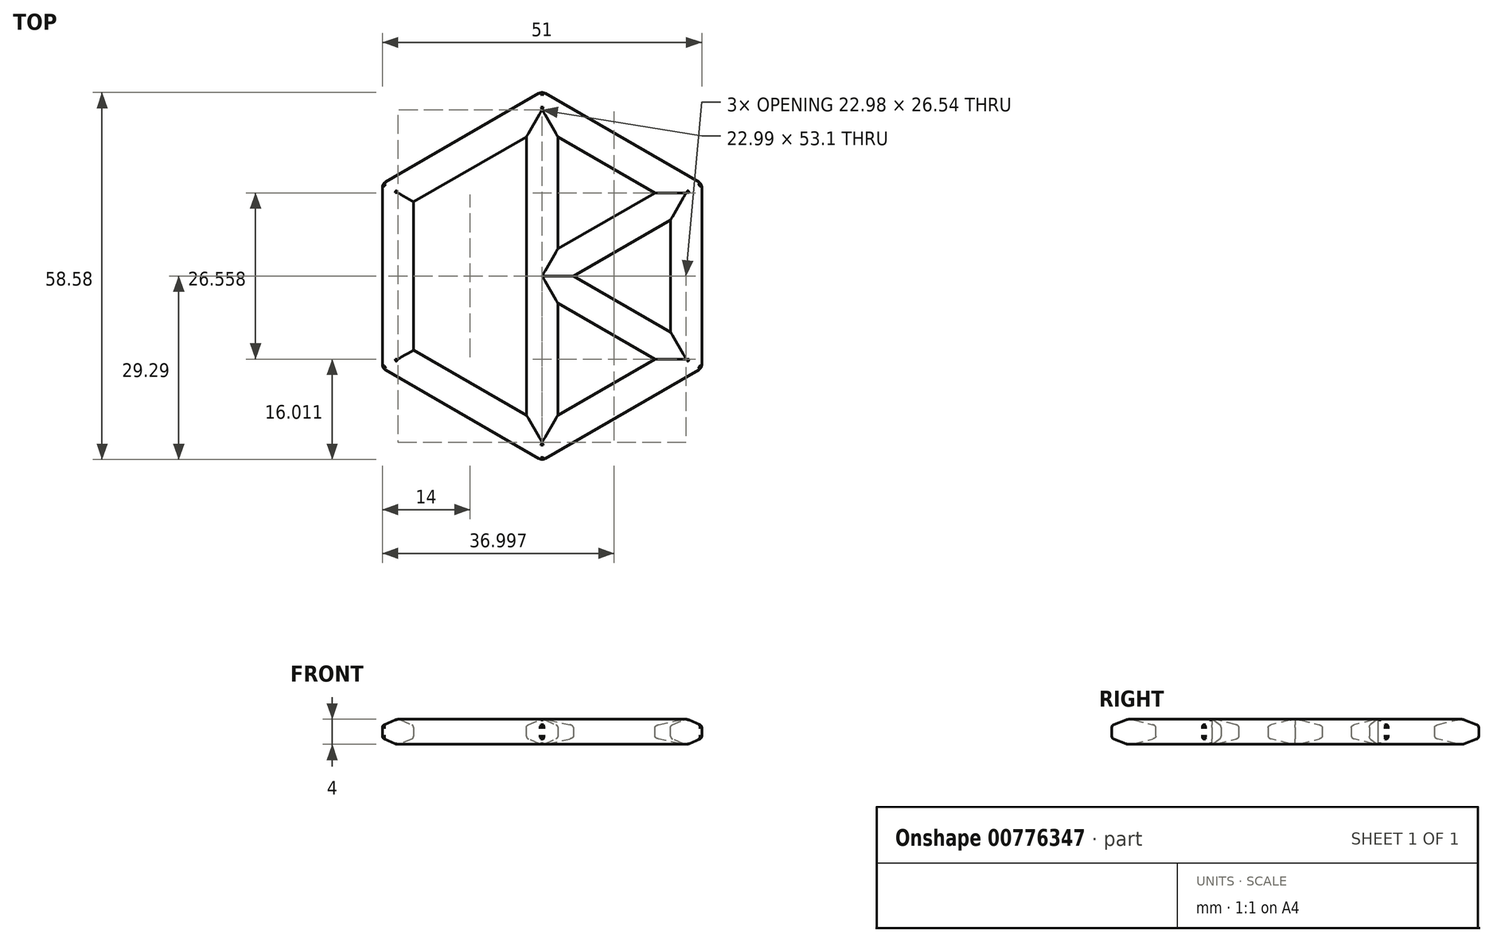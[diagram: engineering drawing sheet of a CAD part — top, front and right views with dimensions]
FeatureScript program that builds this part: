
annotation { "Feature Type Name" : "Feature", "Feature Type Description" : "" }
export const myFeature = defineFeature(function(context is Context, id is Id, definition is map)
    precondition{}
    {
        {
            var Q0;
            Q0=qCreatedBy(makeId("Top.planeOp"),FACE);
            var sketch = newSketch(context, id + "F0", { "sketchPlane" : qUnion([Q0])});
            skCircle(sketch, "E0.cCircle", {"center": v(0, 0) * mm, "radius": 25.5 * mm, "construction": true});
            skLineSegment(sketch, "E0.0", {"start": v(-25.5, -14.72) * mm, "end": v(-25.5, 14.72) * mm});
            skLineSegment(sketch, "E0.1", {"start": v(-25.5, 14.72) * mm, "end": v(0, 29.44) * mm});
            skLineSegment(sketch, "E0.2", {"start": v(0, 29.44) * mm, "end": v(25.5, 14.72) * mm});
            skLineSegment(sketch, "E0.3", {"start": v(25.5, 14.72) * mm, "end": v(25.5, -14.72) * mm});
            skLineSegment(sketch, "E0.4", {"start": v(25.5, -14.72) * mm, "end": v(0, -29.44) * mm});
            skLineSegment(sketch, "E0.5", {"start": v(0, -29.44) * mm, "end": v(-25.5, -14.72) * mm});
            skPoint(sketch, "E0.0.midPoint", {"position": v(-25.5, 0) * mm});
            skSolve(sketch);
        }
        {
            var Q0;
            Q0=qCreatedBy(makeId("Front.planeOp"),FACE);
            var sketch = newSketch(context, id + "F1", { "sketchPlane" : qUnion([Q0])});
            skLineSegment(sketch, "E1", {"start": v(-25.5, -1) * mm, "end": v(-25.5, 1) * mm});
            skLineSegment(sketch, "E2", {"start": v(-22.75, 2) * mm, "end": v(-20.5, 1) * mm});
            skLineSegment(sketch, "E3", {"start": v(-20.5, 1) * mm, "end": v(-20.5, -1) * mm});
            skLineSegment(sketch, "E4", {"start": v(-20.5, -1) * mm, "end": v(-22.75, -2) * mm});
            skLineSegment(sketch, "E5", {"start": v(-23.25, 2) * mm, "end": v(-23.25, -2) * mm});
            skLineSegment(sketch, "E6", {"start": v(-22.75, -2) * mm, "end": v(-22.75, 2) * mm});
            skLineSegment(sketch, "E7", {"start": v(-25.5, -1) * mm, "end": v(-23.25, -2) * mm});
            skLineSegment(sketch, "E8", {"start": v(-22.75, -2) * mm, "end": v(-23.25, -2) * mm});
            skLineSegment(sketch, "E9", {"start": v(-23.25, 2) * mm, "end": v(-22.75, 2) * mm});
            skLineSegment(sketch, "E10", {"start": v(-25.5, 1) * mm, "end": v(-23.25, 2) * mm});
            skLineSegment(sketch, "E11", {"start": v(-22.75, 2) * mm, "end": v(-23.25, -2) * mm});
            skPoint(sketch, "E12", {"position": v(-23, 0) * mm});
            skSolve(sketch);
        }
        {
            var Q0;
            Q0=makeQuery(id+"F1.imprint","IMPRINT",FACE,{"disambiguationData":[TD([[makeQuery(id+"F1.imprint","IMPRINT",EDGE,{"derivedFrom":sQuery(id+"F1.wireOp",EDGE,"E1")}),-1.0]])]});
            var Q1;
            Q1=makeQuery(id+"F1.imprint","IMPRINT",FACE,{"disambiguationData":[TD([[makeQuery(id+"F1.imprint","IMPRINT",EDGE,{"derivedFrom":sQuery(id+"F1.wireOp",EDGE,"E5")}),1.0]])]});
            var Q2;
            Q2=makeQuery(id+"F1.imprint","IMPRINT",FACE,{"disambiguationData":[TD([[makeQuery(id+"F1.imprint","IMPRINT",EDGE,{"derivedFrom":sQuery(id+"F1.wireOp",EDGE,"E6")}),1.0]])]});
            var Q3;
            Q3=makeQuery(id+"F1.imprint","IMPRINT",FACE,{"disambiguationData":[TD([[makeQuery(id+"F1.imprint","IMPRINT",EDGE,{"derivedFrom":sQuery(id+"F1.wireOp",EDGE,"E2")}),-1.0]])]});
            var Q4;
            Q4=sQuery(id+"F0.wireOp",EDGE,"E0.3");
            var Q5;
            Q5=sQuery(id+"F0.wireOp",EDGE,"E0.2");
            var Q6;
            Q6=sQuery(id+"F0.wireOp",EDGE,"E0.1");
            var Q7;
            Q7=sQuery(id+"F0.wireOp",EDGE,"E0.0");
            var Q8;
            Q8=sQuery(id+"F0.wireOp",EDGE,"E0.5");
            var Q9;
            Q9=sQuery(id+"F0.wireOp",EDGE,"E0.4");
            sweep(context, id + "F2", {"profiles" : qUnion([Q0, Q1, Q2, Q3]), "path" : qUnion([Q4, Q5, Q6, Q7, Q8, Q9])});
        }
        {
            var Q0;
            Q0=qCreatedBy(makeId("Front.planeOp"),FACE);
            var sketch = newSketch(context, id + "F3", { "sketchPlane" : qUnion([Q0])});
            skLineSegment(sketch, "E13", {"start": v(-2.5, -1) * mm, "end": v(-2.5, 1) * mm});
            skLineSegment(sketch, "E14", {"start": v(0.25, 2) * mm, "end": v(2.5, 1) * mm});
            skLineSegment(sketch, "E15", {"start": v(2.5, 1) * mm, "end": v(2.5, -1) * mm});
            skLineSegment(sketch, "E16", {"start": v(2.5, -1) * mm, "end": v(0.25, -2) * mm});
            skLineSegment(sketch, "E17", {"start": v(-0.25, 2) * mm, "end": v(-0.25, -2) * mm});
            skLineSegment(sketch, "E18", {"start": v(0.25, -2) * mm, "end": v(0.25, 2) * mm});
            skLineSegment(sketch, "E19", {"start": v(-2.5, -1) * mm, "end": v(-0.25, -2) * mm});
            skLineSegment(sketch, "E20", {"start": v(0.25, -2) * mm, "end": v(-0.25, -2) * mm});
            skLineSegment(sketch, "E21", {"start": v(-0.25, 2) * mm, "end": v(0.25, 2) * mm});
            skLineSegment(sketch, "E22", {"start": v(-2.5, 1) * mm, "end": v(-0.25, 2) * mm});
            skLineSegment(sketch, "E23", {"start": v(0, 2) * mm, "end": v(0, -2) * mm});
            skPoint(sketch, "E24", {"position": v(0, 0) * mm});
            skSolve(sketch);
        }
        {
            var Q0;
            Q0=qSketchRegion(id+"F3",true);
            extrude(context, id + "F4", {"entities" : qUnion([Q0]), "endBound" : BoundingType.UP_TO_NEXT, "depth" : 25 * mm, "offsetDistance" : 25 * mm});
        }
        {
            var Q0;
            Q0=makeQuery(id+"F4.opExtrude","SWEPT_BODY",BODY,{"disambiguationData":[OSD([sQuery(id+"F3.wireOp",EDGE,"E13"),sQuery(id+"F3.wireOp",EDGE,"E14"),sQuery(id+"F3.wireOp",EDGE,"E15"),sQuery(id+"F3.wireOp",EDGE,"E16"),sQuery(id+"F3.wireOp",EDGE,"E19"),sQuery(id+"F3.wireOp",EDGE,"E20"),sQuery(id+"F3.wireOp",EDGE,"E21"),sQuery(id+"F3.wireOp",EDGE,"E22")])]});
            var Q1;
            Q1=sQuery(id+"F3.wireOp",EDGE,"E23");
            circularPattern(context, id + "F5", {"operationType" : NewBodyOperationType.ADD, "entities" : qUnion([Q0]), "axis" : qUnion([Q1]), "angle" : 180 * degree, "instanceCount" : 4, "oppositeDirection" : true, "equalSpace" : true});
        }
        {
            var Q0;
            Q0=makeQuery(id+"F2.opSweep","MID_CAP_EDGE",EDGE,{"disambiguationData":[OSD([sQuery(id+"F0.wireOp",VERTEX,"E0.4.start"),sQuery(id+"F1.wireOp",EDGE,"E1")])],"capPos":2.0});
            var Q1;
            Q1=makeQuery(id+"F2.opSweep","MID_CAP_EDGE",EDGE,{"disambiguationData":[OSD([sQuery(id+"F0.wireOp",VERTEX,"E0.4.start"),sQuery(id+"F1.wireOp",EDGE,"E10")])],"capPos":2.0});
            var Q2;
            Q2=makeQuery(id+"F2.opSweep","MID_CAP_EDGE",EDGE,{"disambiguationData":[OSD([sQuery(id+"F0.wireOp",VERTEX,"E0.4.start"),sQuery(id+"F1.wireOp",EDGE,"E7")])],"capPos":2.0});
            var Q3;
            Q3=makeQuery(id+"F2.opSweep","MID_CAP_EDGE",EDGE,{"disambiguationData":[OSD([sQuery(id+"F0.wireOp",VERTEX,"E0.2.end"),sQuery(id+"F1.wireOp",EDGE,"E10")])],"capPos":3.0});
            var Q4;
            Q4=makeQuery(id+"F2.opSweep","MID_CAP_EDGE",EDGE,{"disambiguationData":[OSD([sQuery(id+"F0.wireOp",VERTEX,"E0.2.end"),sQuery(id+"F1.wireOp",EDGE,"E1")])],"capPos":3.0});
            var Q5;
            Q5=makeQuery(id+"F2.opSweep","MID_CAP_EDGE",EDGE,{"disambiguationData":[OSD([sQuery(id+"F0.wireOp",VERTEX,"E0.2.end"),sQuery(id+"F1.wireOp",EDGE,"E7")])],"capPos":3.0});
            var Q6;
            Q6=makeQuery(id+"F2.opSweep","MID_CAP_EDGE",EDGE,{"disambiguationData":[OSD([sQuery(id+"F0.wireOp",VERTEX,"E0.1.end"),sQuery(id+"F1.wireOp",EDGE,"E7")])],"capPos":4.0});
            var Q7;
            Q7=makeQuery(id+"F2.opSweep","MID_CAP_EDGE",EDGE,{"disambiguationData":[OSD([sQuery(id+"F0.wireOp",VERTEX,"E0.1.end"),sQuery(id+"F1.wireOp",EDGE,"E1")])],"capPos":4.0});
            var Q8;
            Q8=makeQuery(id+"F2.opSweep","MID_CAP_EDGE",EDGE,{"disambiguationData":[OSD([sQuery(id+"F0.wireOp",VERTEX,"E0.1.end"),sQuery(id+"F1.wireOp",EDGE,"E10")])],"capPos":4.0});
            var Q9;
            Q9=makeQuery(id+"F2.opSweep","MID_CAP_EDGE",EDGE,{"disambiguationData":[OSD([sQuery(id+"F0.wireOp",VERTEX,"E0.0.end"),sQuery(id+"F1.wireOp",EDGE,"E1")])],"capPos":5.0});
            var Q10;
            Q10=makeQuery(id+"F2.opSweep","MID_CAP_EDGE",EDGE,{"disambiguationData":[OSD([sQuery(id+"F0.wireOp",VERTEX,"E0.0.end"),sQuery(id+"F1.wireOp",EDGE,"E10")])],"capPos":5.0});
            var Q11;
            Q11=makeQuery(id+"F2.opSweep","MID_CAP_EDGE",EDGE,{"disambiguationData":[OSD([sQuery(id+"F0.wireOp",VERTEX,"E0.0.end"),sQuery(id+"F1.wireOp",EDGE,"E7")])],"capPos":5.0});
            var Q12;
            Q12=makeQuery(id+"F2.opSweep","CAP_EDGE",EDGE,{"disambiguationData":[OSD([sQuery(id+"F0.wireOp",VERTEX,"E0.5.end"),sQuery(id+"F1.wireOp",EDGE,"E7")])],"isStart":true});
            var Q13;
            Q13=makeQuery(id+"F2.opSweep","CAP_EDGE",EDGE,{"disambiguationData":[OSD([sQuery(id+"F0.wireOp",VERTEX,"E0.5.end"),sQuery(id+"F1.wireOp",EDGE,"E1")])],"isStart":true});
            var Q14;
            Q14=makeQuery(id+"F2.opSweep","CAP_EDGE",EDGE,{"disambiguationData":[OSD([sQuery(id+"F0.wireOp",VERTEX,"E0.5.end"),sQuery(id+"F1.wireOp",EDGE,"E10")])],"isStart":true});
            var Q15;
            Q15=makeQuery(id+"F2.opSweep","MID_CAP_EDGE",EDGE,{"disambiguationData":[OSD([sQuery(id+"F0.wireOp",VERTEX,"E0.4.end"),sQuery(id+"F1.wireOp",EDGE,"E10")])],"capPos":1.0});
            var Q16;
            Q16=makeQuery(id+"F2.opSweep","MID_CAP_EDGE",EDGE,{"disambiguationData":[OSD([sQuery(id+"F0.wireOp",VERTEX,"E0.4.end"),sQuery(id+"F1.wireOp",EDGE,"E1")])],"capPos":1.0});
            var Q17;
            Q17=makeQuery(id+"F2.opSweep","MID_CAP_EDGE",EDGE,{"disambiguationData":[OSD([sQuery(id+"F0.wireOp",VERTEX,"E0.4.end"),sQuery(id+"F1.wireOp",EDGE,"E7")])],"capPos":1.0});
            fillet(context, id + "F6", {"entities" : qUnion([Q0, Q1, Q2, Q3, Q4, Q5, Q6, Q7, Q8, Q9, Q10, Q11, Q12, Q13, Q14, Q15, Q16, Q17]), "radius" : 1 * mm, "tangentPropagation" : true, "allowEdgeOverflow" : false});
        }
        {
            var Q0;
            Q0=makeQuery(id+"F2.opSweep","SWEPT_EDGE",EDGE,{"disambiguationData":[OSD([sQuery(id+"F0.wireOp",EDGE,"E0.2"),sQuery(id+"F1.wireOp",EDGE,"E1"),sQuery(id+"F1.wireOp",EDGE,"E10")])]});
            var Q1;
            Q1=makeQuery(id+"F2.opSweep","SWEPT_EDGE",EDGE,{"disambiguationData":[OSD([sQuery(id+"F0.wireOp",EDGE,"E0.1"),sQuery(id+"F1.wireOp",EDGE,"E1"),sQuery(id+"F1.wireOp",EDGE,"E10")])]});
            var Q2;
            Q2=makeQuery(id+"F2.opSweep","SWEPT_EDGE",EDGE,{"disambiguationData":[OSD([sQuery(id+"F0.wireOp",EDGE,"E0.0"),sQuery(id+"F1.wireOp",EDGE,"E1"),sQuery(id+"F1.wireOp",EDGE,"E10")])]});
            var Q3;
            Q3=makeQuery(id+"F2.opSweep","SWEPT_EDGE",EDGE,{"disambiguationData":[OSD([sQuery(id+"F0.wireOp",EDGE,"E0.5"),sQuery(id+"F1.wireOp",EDGE,"E1"),sQuery(id+"F1.wireOp",EDGE,"E10")])]});
            var Q4;
            Q4=makeQuery(id+"F2.opSweep","SWEPT_EDGE",EDGE,{"disambiguationData":[OSD([sQuery(id+"F0.wireOp",EDGE,"E0.1"),sQuery(id+"F1.wireOp",EDGE,"E1"),sQuery(id+"F1.wireOp",EDGE,"E7")])]});
            var Q5;
            Q5=makeQuery(id+"F2.opSweep","SWEPT_EDGE",EDGE,{"disambiguationData":[OSD([sQuery(id+"F0.wireOp",EDGE,"E0.0"),sQuery(id+"F1.wireOp",EDGE,"E1"),sQuery(id+"F1.wireOp",EDGE,"E7")])]});
            var Q6;
            Q6=makeQuery(id+"F2.opSweep","SWEPT_EDGE",EDGE,{"disambiguationData":[OSD([sQuery(id+"F0.wireOp",EDGE,"E0.5"),sQuery(id+"F1.wireOp",EDGE,"E1"),sQuery(id+"F1.wireOp",EDGE,"E7")])]});
            var Q7;
            Q7=makeQuery(id+"F2.opSweep","SWEPT_EDGE",EDGE,{"disambiguationData":[OSD([sQuery(id+"F0.wireOp",EDGE,"E0.4"),sQuery(id+"F1.wireOp",EDGE,"E1"),sQuery(id+"F1.wireOp",EDGE,"E10")])]});
            var Q8;
            Q8=makeQuery(id+"F2.opSweep","SWEPT_EDGE",EDGE,{"disambiguationData":[OSD([sQuery(id+"F0.wireOp",EDGE,"E0.3"),sQuery(id+"F1.wireOp",EDGE,"E1"),sQuery(id+"F1.wireOp",EDGE,"E10")])]});
            var Q9;
            Q9=makeQuery(id+"F2.opSweep","SWEPT_EDGE",EDGE,{"disambiguationData":[OSD([sQuery(id+"F0.wireOp",EDGE,"E0.4"),sQuery(id+"F1.wireOp",EDGE,"E1"),sQuery(id+"F1.wireOp",EDGE,"E7")])]});
            var Q10;
            Q10=makeQuery(id+"F2.opSweep","SWEPT_EDGE",EDGE,{"disambiguationData":[OSD([sQuery(id+"F0.wireOp",EDGE,"E0.3"),sQuery(id+"F1.wireOp",EDGE,"E1"),sQuery(id+"F1.wireOp",EDGE,"E7")])]});
            var Q11;
            Q11=makeQuery(id+"F2.opSweep","SWEPT_EDGE",EDGE,{"disambiguationData":[OSD([sQuery(id+"F0.wireOp",EDGE,"E0.2"),sQuery(id+"F1.wireOp",EDGE,"E1"),sQuery(id+"F1.wireOp",EDGE,"E7")])]});
            var Q12;
            Q12=makeQuery(id+"F5.opPattern","COPY",EDGE,{"derivedFrom":makeQuery(id+"F4.opExtrude","SWEPT_EDGE",EDGE,{"disambiguationData":[OSD([sQuery(id+"F3.wireOp",EDGE,"E13"),sQuery(id+"F3.wireOp",EDGE,"E19")])]}),"instanceName":"3"});
            var Q13;
            Q13=makeQuery(id+"F5.opPattern","COPY",EDGE,{"derivedFrom":makeQuery(id+"F4.opExtrude","SWEPT_EDGE",EDGE,{"disambiguationData":[OSD([sQuery(id+"F3.wireOp",EDGE,"E13"),sQuery(id+"F3.wireOp",EDGE,"E22")])]}),"instanceName":"3"});
            var Q14;
            Q14=makeQuery(id+"F5.opPattern","COPY",EDGE,{"derivedFrom":makeQuery(id+"F4.opExtrude","SWEPT_EDGE",EDGE,{"disambiguationData":[OSD([sQuery(id+"F3.wireOp",EDGE,"E15"),sQuery(id+"F3.wireOp",EDGE,"E16")])]}),"instanceName":"1"});
            var Q15;
            Q15=makeQuery(id+"F5.opPattern","COPY",EDGE,{"derivedFrom":makeQuery(id+"F4.opExtrude","SWEPT_EDGE",EDGE,{"disambiguationData":[OSD([sQuery(id+"F3.wireOp",EDGE,"E14"),sQuery(id+"F3.wireOp",EDGE,"E15")])]}),"instanceName":"1"});
            var Q16;
            Q16=makeQuery(id+"F4.opExtrude","SWEPT_EDGE",EDGE,{"disambiguationData":[OSD([sQuery(id+"F3.wireOp",EDGE,"E15"),sQuery(id+"F3.wireOp",EDGE,"E16")])]});
            var Q17;
            Q17=makeQuery(id+"F2.opSweep","SWEPT_EDGE",EDGE,{"disambiguationData":[OSD([sQuery(id+"F0.wireOp",EDGE,"E0.4"),sQuery(id+"F1.wireOp",EDGE,"E3"),sQuery(id+"F1.wireOp",EDGE,"E4")])]});
            var Q18;
            Q18=makeQuery(id+"F2.opSweep","SWEPT_EDGE",EDGE,{"disambiguationData":[OSD([sQuery(id+"F0.wireOp",EDGE,"E0.4"),sQuery(id+"F1.wireOp",EDGE,"E2"),sQuery(id+"F1.wireOp",EDGE,"E3")])]});
            var Q19;
            Q19=makeQuery(id+"F4.opExtrude","SWEPT_EDGE",EDGE,{"disambiguationData":[OSD([sQuery(id+"F3.wireOp",EDGE,"E14"),sQuery(id+"F3.wireOp",EDGE,"E15")])]});
            var Q20;
            Q20=makeQuery(id+"F5.opPattern","COPY",EDGE,{"derivedFrom":makeQuery(id+"F4.opExtrude","SWEPT_EDGE",EDGE,{"disambiguationData":[OSD([sQuery(id+"F3.wireOp",EDGE,"E15"),sQuery(id+"F3.wireOp",EDGE,"E16")])]}),"instanceName":"2"});
            var Q21;
            Q21=makeQuery(id+"F5.opPattern","COPY",EDGE,{"derivedFrom":makeQuery(id+"F4.opExtrude","SWEPT_EDGE",EDGE,{"disambiguationData":[OSD([sQuery(id+"F3.wireOp",EDGE,"E14"),sQuery(id+"F3.wireOp",EDGE,"E15")])]}),"instanceName":"2"});
            var Q22;
            Q22=makeQuery(id+"F2.opSweep","SWEPT_EDGE",EDGE,{"disambiguationData":[OSD([sQuery(id+"F0.wireOp",EDGE,"E0.3"),sQuery(id+"F1.wireOp",EDGE,"E3"),sQuery(id+"F1.wireOp",EDGE,"E4")])]});
            var Q23;
            Q23=makeQuery(id+"F2.opSweep","SWEPT_EDGE",EDGE,{"disambiguationData":[OSD([sQuery(id+"F0.wireOp",EDGE,"E0.3"),sQuery(id+"F1.wireOp",EDGE,"E2"),sQuery(id+"F1.wireOp",EDGE,"E3")])]});
            var Q24;
            Q24=makeQuery(id+"F5.opPattern","COPY",EDGE,{"derivedFrom":makeQuery(id+"F4.opExtrude","SWEPT_EDGE",EDGE,{"disambiguationData":[OSD([sQuery(id+"F3.wireOp",EDGE,"E13"),sQuery(id+"F3.wireOp",EDGE,"E19")])]}),"instanceName":"1"});
            var Q25;
            Q25=makeQuery(id+"F5.opPattern","COPY",EDGE,{"derivedFrom":makeQuery(id+"F4.opExtrude","SWEPT_EDGE",EDGE,{"disambiguationData":[OSD([sQuery(id+"F3.wireOp",EDGE,"E13"),sQuery(id+"F3.wireOp",EDGE,"E22")])]}),"instanceName":"1"});
            var Q26;
            Q26=makeQuery(id+"F5.opPattern","COPY",EDGE,{"derivedFrom":makeQuery(id+"F4.opExtrude","SWEPT_EDGE",EDGE,{"disambiguationData":[OSD([sQuery(id+"F3.wireOp",EDGE,"E13"),sQuery(id+"F3.wireOp",EDGE,"E22")])]}),"instanceName":"2"});
            var Q27;
            Q27=makeQuery(id+"F5.opPattern","COPY",EDGE,{"derivedFrom":makeQuery(id+"F4.opExtrude","SWEPT_EDGE",EDGE,{"disambiguationData":[OSD([sQuery(id+"F3.wireOp",EDGE,"E13"),sQuery(id+"F3.wireOp",EDGE,"E19")])]}),"instanceName":"2"});
            var Q28;
            Q28=makeQuery(id+"F2.opSweep","SWEPT_EDGE",EDGE,{"disambiguationData":[OSD([sQuery(id+"F0.wireOp",EDGE,"E0.2"),sQuery(id+"F1.wireOp",EDGE,"E3"),sQuery(id+"F1.wireOp",EDGE,"E4")])]});
            var Q29;
            Q29=makeQuery(id+"F2.opSweep","SWEPT_EDGE",EDGE,{"disambiguationData":[OSD([sQuery(id+"F0.wireOp",EDGE,"E0.2"),sQuery(id+"F1.wireOp",EDGE,"E2"),sQuery(id+"F1.wireOp",EDGE,"E3")])]});
            var Q30;
            Q30=makeQuery(id+"F2.opSweep","SWEPT_EDGE",EDGE,{"disambiguationData":[OSD([sQuery(id+"F0.wireOp",EDGE,"E0.0"),sQuery(id+"F1.wireOp",EDGE,"E2"),sQuery(id+"F1.wireOp",EDGE,"E3")])]});
            var Q31;
            Q31=makeQuery(id+"F2.opSweep","SWEPT_EDGE",EDGE,{"disambiguationData":[OSD([sQuery(id+"F0.wireOp",EDGE,"E0.1"),sQuery(id+"F1.wireOp",EDGE,"E2"),sQuery(id+"F1.wireOp",EDGE,"E3")])]});
            var Q32;
            Q32=makeQuery(id+"F2.opSweep","SWEPT_EDGE",EDGE,{"disambiguationData":[OSD([sQuery(id+"F0.wireOp",EDGE,"E0.5"),sQuery(id+"F1.wireOp",EDGE,"E2"),sQuery(id+"F1.wireOp",EDGE,"E3")])]});
            var Q33;
            Q33=makeQuery(id+"F2.opSweep","SWEPT_EDGE",EDGE,{"disambiguationData":[OSD([sQuery(id+"F0.wireOp",EDGE,"E0.5"),sQuery(id+"F1.wireOp",EDGE,"E3"),sQuery(id+"F1.wireOp",EDGE,"E4")])]});
            var Q34;
            Q34=makeQuery(id+"F2.opSweep","SWEPT_EDGE",EDGE,{"disambiguationData":[OSD([sQuery(id+"F0.wireOp",EDGE,"E0.0"),sQuery(id+"F1.wireOp",EDGE,"E3"),sQuery(id+"F1.wireOp",EDGE,"E4")])]});
            var Q35;
            Q35=makeQuery(id+"F2.opSweep","SWEPT_EDGE",EDGE,{"disambiguationData":[OSD([sQuery(id+"F0.wireOp",EDGE,"E0.1"),sQuery(id+"F1.wireOp",EDGE,"E3"),sQuery(id+"F1.wireOp",EDGE,"E4")])]});
            var Q36;
            Q36=makeQuery(id+"F5.boolean.opBoolean","MERGE",EDGE,{"derivedFrom":[makeQuery(id+"F4.opExtrude","SWEPT_EDGE",EDGE,{"disambiguationData":[OSD([sQuery(id+"F3.wireOp",EDGE,"E13"),sQuery(id+"F3.wireOp",EDGE,"E19")])]}),makeQuery(id+"F5.opPattern","COPY",EDGE,{"derivedFrom":makeQuery(id+"F4.opExtrude","SWEPT_EDGE",EDGE,{"disambiguationData":[OSD([sQuery(id+"F3.wireOp",EDGE,"E15"),sQuery(id+"F3.wireOp",EDGE,"E16")])]}),"instanceName":"3"})]});
            var Q37;
            Q37=makeQuery(id+"F5.boolean.opBoolean","MERGE",EDGE,{"derivedFrom":[makeQuery(id+"F4.opExtrude","SWEPT_EDGE",EDGE,{"disambiguationData":[OSD([sQuery(id+"F3.wireOp",EDGE,"E13"),sQuery(id+"F3.wireOp",EDGE,"E22")])]}),makeQuery(id+"F5.opPattern","COPY",EDGE,{"derivedFrom":makeQuery(id+"F4.opExtrude","SWEPT_EDGE",EDGE,{"disambiguationData":[OSD([sQuery(id+"F3.wireOp",EDGE,"E14"),sQuery(id+"F3.wireOp",EDGE,"E15")])]}),"instanceName":"3"})]});
            fillet(context, id + "F7", {"entities" : qUnion([Q0, Q1, Q2, Q3, Q4, Q5, Q6, Q7, Q8, Q9, Q10, Q11, Q12, Q13, Q14, Q15, Q16, Q17, Q18, Q19, Q20, Q21, Q22, Q23, Q24, Q25, Q26, Q27, Q28, Q29, Q30, Q31, Q32, Q33, Q34, Q35, Q36, Q37]), "radius" : .5 * mm, "tangentPropagation" : true, "allowEdgeOverflow" : false});
        }
        {
            var Q0;
            Q0=makeQuery(id+"F2.opSweep","SWEPT_EDGE",EDGE,{"disambiguationData":[OSD([sQuery(id+"F0.wireOp",EDGE,"E0.1"),sQuery(id+"F1.wireOp",EDGE,"E2"),sQuery(id+"F1.wireOp",EDGE,"E6"),sQuery(id+"F1.wireOp",EDGE,"E9"),sQuery(id+"F1.wireOp",EDGE,"E11")])]});
            var Q1;
            {var subQ0=sQuery(id+"F3.wireOp",EDGE,"E21");Q1=makeQuery(id+"F5.boolean.opBoolean","MERGE",EDGE,{"derivedFrom":[makeQuery(id+"F4.opExtrude","SWEPT_EDGE",EDGE,{"disambiguationData":[OSD([sQuery(id+"F3.wireOp",EDGE,"E17"),subQ0,sQuery(id+"F3.wireOp",EDGE,"E22")])]}),makeQuery(id+"F5.opPattern","COPY",EDGE,{"derivedFrom":makeQuery(id+"F4.opExtrude","SWEPT_EDGE",EDGE,{"disambiguationData":[OSD([sQuery(id+"F3.wireOp",EDGE,"E14"),sQuery(id+"F3.wireOp",EDGE,"E18"),subQ0])]}),"instanceName":"3"})]});}
            var Q2;
            Q2=makeQuery(id+"F2.opSweep","SWEPT_EDGE",EDGE,{"disambiguationData":[OSD([sQuery(id+"F0.wireOp",EDGE,"E0.5"),sQuery(id+"F1.wireOp",EDGE,"E2"),sQuery(id+"F1.wireOp",EDGE,"E6"),sQuery(id+"F1.wireOp",EDGE,"E9"),sQuery(id+"F1.wireOp",EDGE,"E11")])]});
            var Q3;
            Q3=makeQuery(id+"F4.opExtrude","SWEPT_EDGE",EDGE,{"disambiguationData":[OSD([sQuery(id+"F3.wireOp",EDGE,"E14"),sQuery(id+"F3.wireOp",EDGE,"E18"),sQuery(id+"F3.wireOp",EDGE,"E21")])]});
            var Q4;
            Q4=makeQuery(id+"F2.opSweep","SWEPT_EDGE",EDGE,{"disambiguationData":[OSD([sQuery(id+"F0.wireOp",EDGE,"E0.4"),sQuery(id+"F1.wireOp",EDGE,"E2"),sQuery(id+"F1.wireOp",EDGE,"E6"),sQuery(id+"F1.wireOp",EDGE,"E9"),sQuery(id+"F1.wireOp",EDGE,"E11")])]});
            var Q5;
            Q5=makeQuery(id+"F5.opPattern","COPY",EDGE,{"derivedFrom":makeQuery(id+"F4.opExtrude","SWEPT_EDGE",EDGE,{"disambiguationData":[OSD([sQuery(id+"F3.wireOp",EDGE,"E17"),sQuery(id+"F3.wireOp",EDGE,"E21"),sQuery(id+"F3.wireOp",EDGE,"E22")])]}),"instanceName":"1"});
            var Q6;
            Q6=makeQuery(id+"F5.opPattern","COPY",EDGE,{"derivedFrom":makeQuery(id+"F4.opExtrude","SWEPT_EDGE",EDGE,{"disambiguationData":[OSD([sQuery(id+"F3.wireOp",EDGE,"E14"),sQuery(id+"F3.wireOp",EDGE,"E18"),sQuery(id+"F3.wireOp",EDGE,"E21")])]}),"instanceName":"1"});
            var Q7;
            Q7=makeQuery(id+"F5.opPattern","COPY",EDGE,{"derivedFrom":makeQuery(id+"F4.opExtrude","SWEPT_EDGE",EDGE,{"disambiguationData":[OSD([sQuery(id+"F3.wireOp",EDGE,"E17"),sQuery(id+"F3.wireOp",EDGE,"E21"),sQuery(id+"F3.wireOp",EDGE,"E22")])]}),"instanceName":"2"});
            var Q8;
            Q8=makeQuery(id+"F5.opPattern","COPY",EDGE,{"derivedFrom":makeQuery(id+"F4.opExtrude","SWEPT_EDGE",EDGE,{"disambiguationData":[OSD([sQuery(id+"F3.wireOp",EDGE,"E17"),sQuery(id+"F3.wireOp",EDGE,"E21"),sQuery(id+"F3.wireOp",EDGE,"E22")])]}),"instanceName":"3"});
            var Q9;
            Q9=makeQuery(id+"F5.opPattern","COPY",EDGE,{"derivedFrom":makeQuery(id+"F4.opExtrude","SWEPT_EDGE",EDGE,{"disambiguationData":[OSD([sQuery(id+"F3.wireOp",EDGE,"E14"),sQuery(id+"F3.wireOp",EDGE,"E18"),sQuery(id+"F3.wireOp",EDGE,"E21")])]}),"instanceName":"2"});
            var Q10;
            Q10=makeQuery(id+"F2.opSweep","SWEPT_EDGE",EDGE,{"disambiguationData":[OSD([sQuery(id+"F0.wireOp",EDGE,"E0.2"),sQuery(id+"F1.wireOp",EDGE,"E2"),sQuery(id+"F1.wireOp",EDGE,"E6"),sQuery(id+"F1.wireOp",EDGE,"E9"),sQuery(id+"F1.wireOp",EDGE,"E11")])]});
            var Q11;
            Q11=makeQuery(id+"F2.opSweep","SWEPT_EDGE",EDGE,{"disambiguationData":[OSD([sQuery(id+"F0.wireOp",EDGE,"E0.0"),sQuery(id+"F1.wireOp",EDGE,"E2"),sQuery(id+"F1.wireOp",EDGE,"E6"),sQuery(id+"F1.wireOp",EDGE,"E9"),sQuery(id+"F1.wireOp",EDGE,"E11")])]});
            var Q12;
            Q12=makeQuery(id+"F2.opSweep","SWEPT_EDGE",EDGE,{"disambiguationData":[OSD([sQuery(id+"F0.wireOp",EDGE,"E0.4"),sQuery(id+"F1.wireOp",EDGE,"E5"),sQuery(id+"F1.wireOp",EDGE,"E9"),sQuery(id+"F1.wireOp",EDGE,"E10")])]});
            var Q13;
            Q13=makeQuery(id+"F2.opSweep","SWEPT_EDGE",EDGE,{"disambiguationData":[OSD([sQuery(id+"F0.wireOp",EDGE,"E0.5"),sQuery(id+"F1.wireOp",EDGE,"E5"),sQuery(id+"F1.wireOp",EDGE,"E9"),sQuery(id+"F1.wireOp",EDGE,"E10")])]});
            var Q14;
            Q14=makeQuery(id+"F2.opSweep","SWEPT_EDGE",EDGE,{"disambiguationData":[OSD([sQuery(id+"F0.wireOp",EDGE,"E0.0"),sQuery(id+"F1.wireOp",EDGE,"E5"),sQuery(id+"F1.wireOp",EDGE,"E9"),sQuery(id+"F1.wireOp",EDGE,"E10")])]});
            var Q15;
            Q15=makeQuery(id+"F2.opSweep","SWEPT_EDGE",EDGE,{"disambiguationData":[OSD([sQuery(id+"F0.wireOp",EDGE,"E0.1"),sQuery(id+"F1.wireOp",EDGE,"E5"),sQuery(id+"F1.wireOp",EDGE,"E9"),sQuery(id+"F1.wireOp",EDGE,"E10")])]});
            var Q16;
            Q16=makeQuery(id+"F2.opSweep","SWEPT_EDGE",EDGE,{"disambiguationData":[OSD([sQuery(id+"F0.wireOp",EDGE,"E0.2"),sQuery(id+"F1.wireOp",EDGE,"E5"),sQuery(id+"F1.wireOp",EDGE,"E9"),sQuery(id+"F1.wireOp",EDGE,"E10")])]});
            var Q17;
            Q17=makeQuery(id+"F2.opSweep","SWEPT_EDGE",EDGE,{"disambiguationData":[OSD([sQuery(id+"F0.wireOp",EDGE,"E0.3"),sQuery(id+"F1.wireOp",EDGE,"E2"),sQuery(id+"F1.wireOp",EDGE,"E6"),sQuery(id+"F1.wireOp",EDGE,"E9"),sQuery(id+"F1.wireOp",EDGE,"E11")])]});
            var Q18;
            Q18=makeQuery(id+"F2.opSweep","SWEPT_EDGE",EDGE,{"disambiguationData":[OSD([sQuery(id+"F0.wireOp",EDGE,"E0.3"),sQuery(id+"F1.wireOp",EDGE,"E5"),sQuery(id+"F1.wireOp",EDGE,"E9"),sQuery(id+"F1.wireOp",EDGE,"E10")])]});
            var Q19;
            Q19=makeQuery(id+"F2.opSweep","SWEPT_EDGE",EDGE,{"disambiguationData":[OSD([sQuery(id+"F0.wireOp",EDGE,"E0.0"),sQuery(id+"F1.wireOp",EDGE,"E5"),sQuery(id+"F1.wireOp",EDGE,"E7"),sQuery(id+"F1.wireOp",EDGE,"E8"),sQuery(id+"F1.wireOp",EDGE,"E11")])]});
            var Q20;
            Q20=makeQuery(id+"F2.opSweep","SWEPT_EDGE",EDGE,{"disambiguationData":[OSD([sQuery(id+"F0.wireOp",EDGE,"E0.1"),sQuery(id+"F1.wireOp",EDGE,"E5"),sQuery(id+"F1.wireOp",EDGE,"E7"),sQuery(id+"F1.wireOp",EDGE,"E8"),sQuery(id+"F1.wireOp",EDGE,"E11")])]});
            var Q21;
            Q21=makeQuery(id+"F2.opSweep","SWEPT_EDGE",EDGE,{"disambiguationData":[OSD([sQuery(id+"F0.wireOp",EDGE,"E0.1"),sQuery(id+"F1.wireOp",EDGE,"E4"),sQuery(id+"F1.wireOp",EDGE,"E6"),sQuery(id+"F1.wireOp",EDGE,"E8")])]});
            var Q22;
            Q22=makeQuery(id+"F2.opSweep","SWEPT_EDGE",EDGE,{"disambiguationData":[OSD([sQuery(id+"F0.wireOp",EDGE,"E0.0"),sQuery(id+"F1.wireOp",EDGE,"E4"),sQuery(id+"F1.wireOp",EDGE,"E6"),sQuery(id+"F1.wireOp",EDGE,"E8")])]});
            var Q23;
            Q23=makeQuery(id+"F2.opSweep","SWEPT_EDGE",EDGE,{"disambiguationData":[OSD([sQuery(id+"F0.wireOp",EDGE,"E0.5"),sQuery(id+"F1.wireOp",EDGE,"E4"),sQuery(id+"F1.wireOp",EDGE,"E6"),sQuery(id+"F1.wireOp",EDGE,"E8")])]});
            var Q24;
            Q24=makeQuery(id+"F2.opSweep","SWEPT_EDGE",EDGE,{"disambiguationData":[OSD([sQuery(id+"F0.wireOp",EDGE,"E0.5"),sQuery(id+"F1.wireOp",EDGE,"E5"),sQuery(id+"F1.wireOp",EDGE,"E7"),sQuery(id+"F1.wireOp",EDGE,"E8"),sQuery(id+"F1.wireOp",EDGE,"E11")])]});
            var Q25;
            Q25=makeQuery(id+"F2.opSweep","SWEPT_EDGE",EDGE,{"disambiguationData":[OSD([sQuery(id+"F0.wireOp",EDGE,"E0.2"),sQuery(id+"F1.wireOp",EDGE,"E5"),sQuery(id+"F1.wireOp",EDGE,"E7"),sQuery(id+"F1.wireOp",EDGE,"E8"),sQuery(id+"F1.wireOp",EDGE,"E11")])]});
            var Q26;
            Q26=makeQuery(id+"F2.opSweep","SWEPT_EDGE",EDGE,{"disambiguationData":[OSD([sQuery(id+"F0.wireOp",EDGE,"E0.2"),sQuery(id+"F1.wireOp",EDGE,"E4"),sQuery(id+"F1.wireOp",EDGE,"E6"),sQuery(id+"F1.wireOp",EDGE,"E8")])]});
            var Q27;
            {var subQ0=sQuery(id+"F3.wireOp",EDGE,"E20");Q27=makeQuery(id+"F5.boolean.opBoolean","MERGE",EDGE,{"derivedFrom":[makeQuery(id+"F4.opExtrude","SWEPT_EDGE",EDGE,{"disambiguationData":[OSD([sQuery(id+"F3.wireOp",EDGE,"E17"),sQuery(id+"F3.wireOp",EDGE,"E19"),subQ0])]}),makeQuery(id+"F5.opPattern","COPY",EDGE,{"derivedFrom":makeQuery(id+"F4.opExtrude","SWEPT_EDGE",EDGE,{"disambiguationData":[OSD([sQuery(id+"F3.wireOp",EDGE,"E16"),sQuery(id+"F3.wireOp",EDGE,"E18"),subQ0])]}),"instanceName":"3"})]});}
            var Q28;
            Q28=makeQuery(id+"F5.opPattern","COPY",EDGE,{"derivedFrom":makeQuery(id+"F4.opExtrude","SWEPT_EDGE",EDGE,{"disambiguationData":[OSD([sQuery(id+"F3.wireOp",EDGE,"E17"),sQuery(id+"F3.wireOp",EDGE,"E19"),sQuery(id+"F3.wireOp",EDGE,"E20")])]}),"instanceName":"3"});
            var Q29;
            Q29=makeQuery(id+"F5.opPattern","COPY",EDGE,{"derivedFrom":makeQuery(id+"F4.opExtrude","SWEPT_EDGE",EDGE,{"disambiguationData":[OSD([sQuery(id+"F3.wireOp",EDGE,"E16"),sQuery(id+"F3.wireOp",EDGE,"E18"),sQuery(id+"F3.wireOp",EDGE,"E20")])]}),"instanceName":"2"});
            var Q30;
            Q30=makeQuery(id+"F5.opPattern","COPY",EDGE,{"derivedFrom":makeQuery(id+"F4.opExtrude","SWEPT_EDGE",EDGE,{"disambiguationData":[OSD([sQuery(id+"F3.wireOp",EDGE,"E17"),sQuery(id+"F3.wireOp",EDGE,"E19"),sQuery(id+"F3.wireOp",EDGE,"E20")])]}),"instanceName":"2"});
            var Q31;
            Q31=makeQuery(id+"F5.opPattern","COPY",EDGE,{"derivedFrom":makeQuery(id+"F4.opExtrude","SWEPT_EDGE",EDGE,{"disambiguationData":[OSD([sQuery(id+"F3.wireOp",EDGE,"E16"),sQuery(id+"F3.wireOp",EDGE,"E18"),sQuery(id+"F3.wireOp",EDGE,"E20")])]}),"instanceName":"1"});
            var Q32;
            Q32=makeQuery(id+"F5.opPattern","COPY",EDGE,{"derivedFrom":makeQuery(id+"F4.opExtrude","SWEPT_EDGE",EDGE,{"disambiguationData":[OSD([sQuery(id+"F3.wireOp",EDGE,"E17"),sQuery(id+"F3.wireOp",EDGE,"E19"),sQuery(id+"F3.wireOp",EDGE,"E20")])]}),"instanceName":"1"});
            var Q33;
            Q33=makeQuery(id+"F2.opSweep","SWEPT_EDGE",EDGE,{"disambiguationData":[OSD([sQuery(id+"F0.wireOp",EDGE,"E0.3"),sQuery(id+"F1.wireOp",EDGE,"E4"),sQuery(id+"F1.wireOp",EDGE,"E6"),sQuery(id+"F1.wireOp",EDGE,"E8")])]});
            var Q34;
            Q34=makeQuery(id+"F2.opSweep","SWEPT_EDGE",EDGE,{"disambiguationData":[OSD([sQuery(id+"F0.wireOp",EDGE,"E0.3"),sQuery(id+"F1.wireOp",EDGE,"E5"),sQuery(id+"F1.wireOp",EDGE,"E7"),sQuery(id+"F1.wireOp",EDGE,"E8"),sQuery(id+"F1.wireOp",EDGE,"E11")])]});
            var Q35;
            Q35=makeQuery(id+"F4.opExtrude","SWEPT_EDGE",EDGE,{"disambiguationData":[OSD([sQuery(id+"F3.wireOp",EDGE,"E16"),sQuery(id+"F3.wireOp",EDGE,"E18"),sQuery(id+"F3.wireOp",EDGE,"E20")])]});
            var Q36;
            Q36=makeQuery(id+"F2.opSweep","SWEPT_EDGE",EDGE,{"disambiguationData":[OSD([sQuery(id+"F0.wireOp",EDGE,"E0.4"),sQuery(id+"F1.wireOp",EDGE,"E4"),sQuery(id+"F1.wireOp",EDGE,"E6"),sQuery(id+"F1.wireOp",EDGE,"E8")])]});
            var Q37;
            Q37=makeQuery(id+"F2.opSweep","SWEPT_EDGE",EDGE,{"disambiguationData":[OSD([sQuery(id+"F0.wireOp",EDGE,"E0.4"),sQuery(id+"F1.wireOp",EDGE,"E5"),sQuery(id+"F1.wireOp",EDGE,"E7"),sQuery(id+"F1.wireOp",EDGE,"E8"),sQuery(id+"F1.wireOp",EDGE,"E11")])]});
            fillet(context, id + "F8", {"entities" : qUnion([Q0, Q1, Q2, Q3, Q4, Q5, Q6, Q7, Q8, Q9, Q10, Q11, Q12, Q13, Q14, Q15, Q16, Q17, Q18, Q19, Q20, Q21, Q22, Q23, Q24, Q25, Q26, Q27, Q28, Q29, Q30, Q31, Q32, Q33, Q34, Q35, Q36, Q37]), "radius" : 1.15 * mm, "allowEdgeOverflow" : false});
        }
    });
